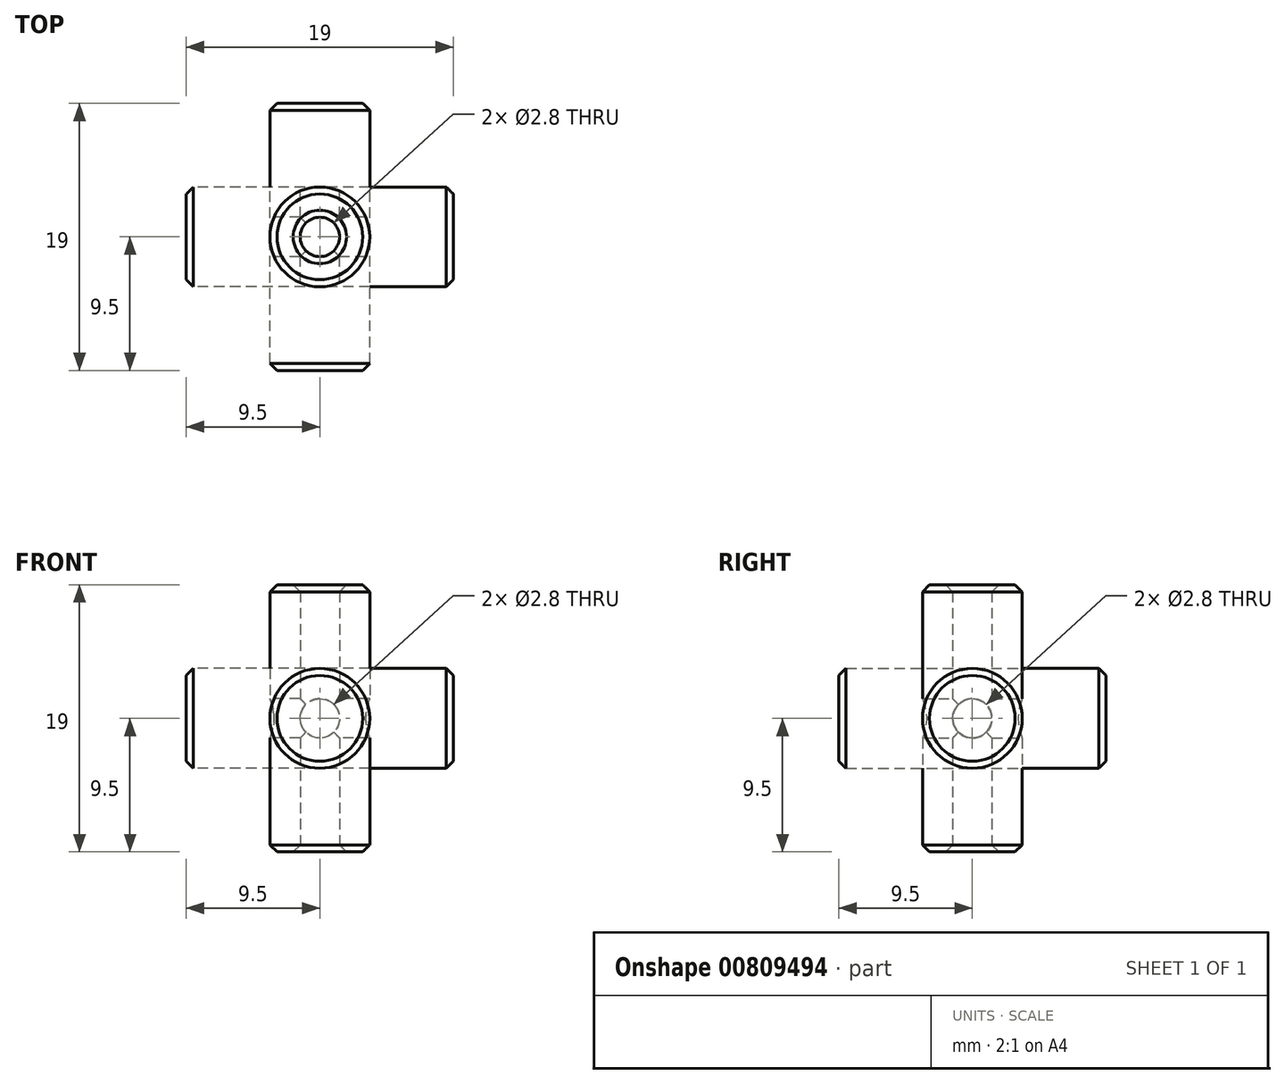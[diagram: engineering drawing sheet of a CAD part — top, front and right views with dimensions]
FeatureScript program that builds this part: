
annotation { "Feature Type Name" : "Feature", "Feature Type Description" : "" }
export const myFeature = defineFeature(function(context is Context, id is Id, definition is map)
    precondition{}
    {
        {
            var Q0;
            Q0=qCreatedBy(makeId("Front.planeOp"),FACE);
            var sketch = newSketch(context, id + "F0", { "sketchPlane" : qUnion([Q0])});
            skCircle(sketch, "E0", {"center": v(0, 0) * mm, "radius": 3.55 * mm});
            skSolve(sketch);
        }
        {
            var Q0;
            Q0=makeQuery(id+"F0.imprint","IMPRINT",FACE,{"disambiguationData":[TD([[makeQuery(id+"F0.imprint","IMPRINT",EDGE,{"derivedFrom":sQuery(id+"F0.wireOp",EDGE,"E0")}),1.0]])]});
            extrude(context, id + "F1", {"entities" : qUnion([Q0]), "endBound" : BoundingType.SYMMETRIC, "depth" : 19 * mm, "offsetDistance" : 25 * mm});
        }
        {
            var Q0;
            Q0=qCreatedBy(makeId("Front.planeOp"),FACE);
            var sketch = newSketch(context, id + "F2", { "sketchPlane" : qUnion([Q0])});
            skCircle(sketch, "E1", {"center": v(0, 0) * mm, "radius": 1.4 * mm});
            skSolve(sketch);
        }
        {
            var Q0;
            Q0 = qSketchRegion(id + "F2", true);
            extrude(context, id + "F3", {"entities" : qUnion([Q0]), "endBound" : BoundingType.SYMMETRIC, "depth" : 20 * mm, "offsetDistance" : 25 * mm});
        }
        {
            var Q0;
            Q0=qCreatedBy(makeId("Front.planeOp"),FACE);
            var sketch = newSketch(context, id + "F4", { "sketchPlane" : qUnion([Q0])});
            skLineSegment(sketch, "E2.bottom", {"start": v(0, 0) * mm, "end": v(10, 0) * mm});
            skLineSegment(sketch, "E2.top", {"start": v(0, 10) * mm, "end": v(10, 10) * mm});
            skLineSegment(sketch, "E2.left", {"start": v(0, 0) * mm, "end": v(0, 10) * mm});
            skLineSegment(sketch, "E2.right", {"start": v(10, 0) * mm, "end": v(10, 10) * mm});
            skSolve(sketch);
        }
        {
            var Q0;
            Q0 = qSketchRegion(id + "F4", true);
            extrude(context, id + "F5", {"entities" : qUnion([Q0]), "depth" : 10 * mm, "offsetDistance" : 25 * mm});
        }
        {
            var Q0;
            Q0=qCreatedBy(makeId("Origin.pointOp"),VERTEX);
            var Q1;
            Q1=makeQuery(id+"F5.opExtrude","CAP_VERTEX",VERTEX,{"disambiguationData":[OSD([sQuery(id+"F4.wireOp",EDGE,"E2.top"),sQuery(id+"F4.wireOp",EDGE,"E2.right")])],"isStart":false});
            var Q2;
            Q2=makeQuery(id+"F5.opExtrude","CAP_VERTEX",VERTEX,{"disambiguationData":[OSD([sQuery(id+"F4.wireOp",EDGE,"E2.bottom"),sQuery(id+"F4.wireOp",EDGE,"E2.right")])],"isStart":false});
            cPlane(context, id + "F6", {"entities" : qUnion([Q0, Q1, Q2]), "cplaneType" : CPlaneType.THREE_POINT, "offset" : 25 * mm, "width" : 150 * mm, "height" : 150 * mm});
        }
        {
            var Q0;
            Q0=qCreatedBy(id+"F6.planeOp",FACE);
            var sketch = newSketch(context, id + "F7", { "sketchPlane" : qUnion([Q0])});
            skLineSegment(sketch, "E3", {"start": v(0, 0) * mm, "end": v(14.14, 10) * mm});
            skSolve(sketch);
        }
        {
            var Q0;
            Q0=makeQuery(id+"F5.opExtrude","SWEPT_BODY",BODY,{"disambiguationData":[OSD([sQuery(id+"F4.wireOp",EDGE,"E2.bottom"),sQuery(id+"F4.wireOp",EDGE,"E2.top"),sQuery(id+"F4.wireOp",EDGE,"E2.left"),sQuery(id+"F4.wireOp",EDGE,"E2.right")])]});
            deleteBodies(context, id + "F8", {"entities" : qUnion([Q0])});
        }
        {
            var Q0;
            Q0=makeQuery(id+"F1.opExtrude","SWEPT_BODY",BODY,{"disambiguationData":[OSD([sQuery(id+"F0.wireOp",EDGE,"E0")])]});
            var Q1;
            Q1=makeQuery(id+"F3.opExtrude","SWEPT_BODY",BODY,{"disambiguationData":[OSD([sQuery(id+"F2.wireOp",EDGE,"E1")])]});
            var Q2;
            Q2=sQuery(id+"F7.wireOp",EDGE,"E3");
            circularPattern(context, id + "F9", {"entities" : qUnion([Q0, Q1]), "axis" : qUnion([Q2]), "angle" : 360 * degree, "instanceCount" : 3, "equalSpace" : true});
        }
        {
            var Q0;
            Q0=makeQuery(id+"F9.opPattern","COPY",BODY,{"derivedFrom":makeQuery(id+"F3.opExtrude","SWEPT_BODY",BODY,{"disambiguationData":[OSD([sQuery(id+"F2.wireOp",EDGE,"E1")])]}),"instanceName":"2"});
            var Q1;
            Q1=makeQuery(id+"F3.opExtrude","SWEPT_BODY",BODY,{"disambiguationData":[OSD([sQuery(id+"F2.wireOp",EDGE,"E1")])]});
            var Q2;
            Q2=makeQuery(id+"F9.opPattern","COPY",BODY,{"derivedFrom":makeQuery(id+"F3.opExtrude","SWEPT_BODY",BODY,{"disambiguationData":[OSD([sQuery(id+"F2.wireOp",EDGE,"E1")])]}),"instanceName":"1"});
            var Q3;
            Q3=makeQuery(id+"F9.opPattern","COPY",BODY,{"derivedFrom":makeQuery(id+"F1.opExtrude","SWEPT_BODY",BODY,{"disambiguationData":[OSD([sQuery(id+"F0.wireOp",EDGE,"E0")])]}),"instanceName":"2"});
            booleanBodies(context, id + "F10", {"operationType" : BooleanOperationType.SUBTRACTION, "tools" : qUnion([Q0, Q1, Q2]), "targets" : qUnion([Q3])});
        }
        {
            var Q0;
            Q0=makeQuery(id+"F9.opPattern","COPY",FACE,{"derivedFrom":makeQuery(id+"F1.opExtrude","CAP_FACE",FACE,{"disambiguationData":[OSD([sQuery(id+"F0.wireOp",EDGE,"E0")])],"isStart":true}),"instanceName":"2"});
            var Q1;
            Q1=makeQuery(id+"F9.opPattern","COPY",FACE,{"derivedFrom":makeQuery(id+"F1.opExtrude","CAP_FACE",FACE,{"disambiguationData":[OSD([sQuery(id+"F0.wireOp",EDGE,"E0")])],"isStart":false}),"instanceName":"1"});
            var Q2;
            Q2=makeQuery(id+"F1.opExtrude","CAP_EDGE",EDGE,{"disambiguationData":[OSD([sQuery(id+"F0.wireOp",EDGE,"E0")])],"isStart":true});
            var Q3;
            Q3=makeQuery(id+"F1.opExtrude","CAP_FACE",FACE,{"disambiguationData":[OSD([sQuery(id+"F0.wireOp",EDGE,"E0")])],"isStart":false});
            var Q4;
            Q4=makeQuery(id+"F9.opPattern","COPY",FACE,{"derivedFrom":makeQuery(id+"F1.opExtrude","CAP_FACE",FACE,{"disambiguationData":[OSD([sQuery(id+"F0.wireOp",EDGE,"E0")])],"isStart":true}),"instanceName":"1"});
            var Q5;
            Q5=makeQuery(id+"F9.opPattern","COPY",FACE,{"derivedFrom":makeQuery(id+"F1.opExtrude","CAP_FACE",FACE,{"disambiguationData":[OSD([sQuery(id+"F0.wireOp",EDGE,"E0")])],"isStart":false}),"instanceName":"2"});
            chamfer(context, id + "F11", {"entities" : qUnion([Q0, Q1, Q2, Q3, Q4, Q5]), "width" : 0.5 * mm});
        }
    });
